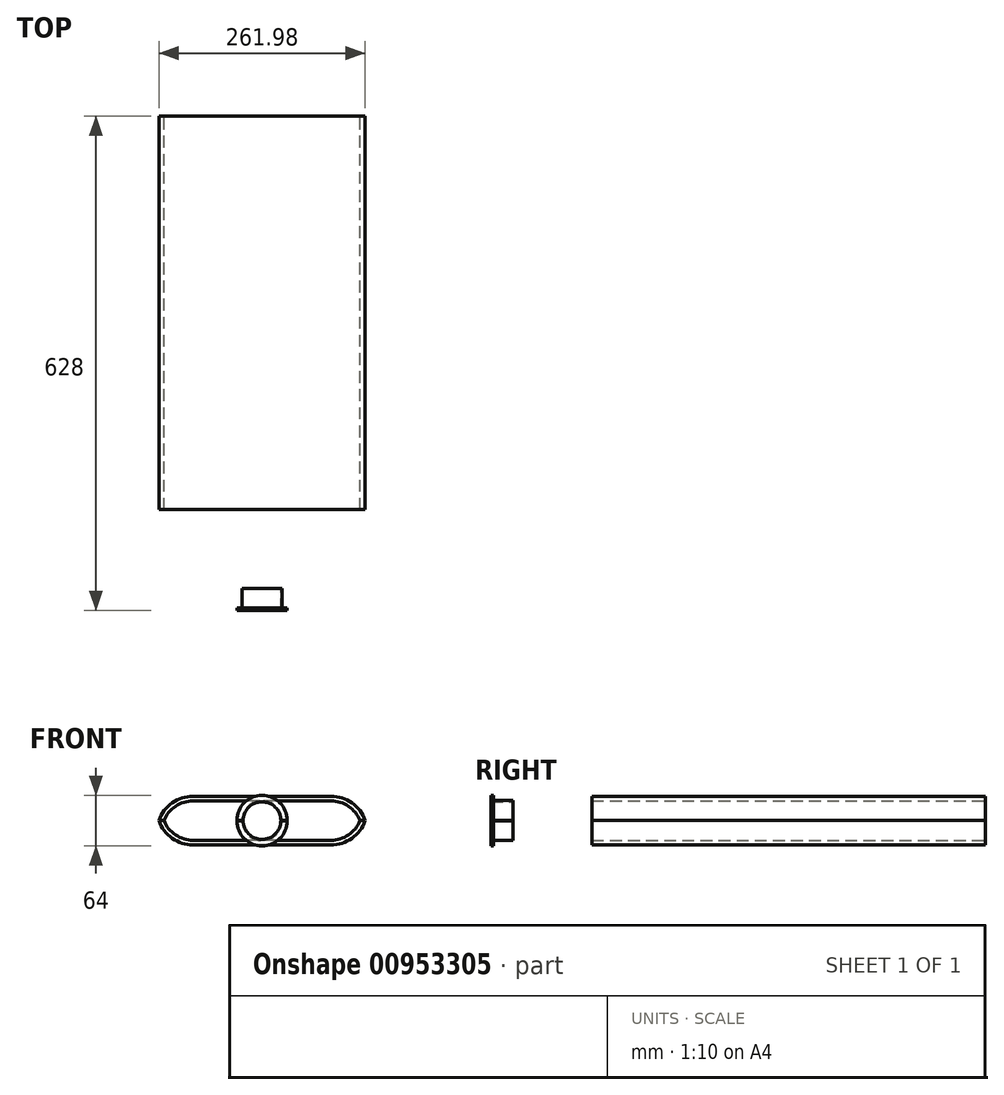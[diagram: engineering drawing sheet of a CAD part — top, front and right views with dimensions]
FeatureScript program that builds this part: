
annotation { "Feature Type Name" : "Feature", "Feature Type Description" : "" }
export const myFeature = defineFeature(function(context is Context, id is Id, definition is map)
    precondition{}
    {
        {
            var Q0;
            Q0=qCreatedBy(makeId("Front.planeOp"),FACE);
            var sketch = newSketch(context, id + "F0", { "sketchPlane" : qUnion([Q0])});
            skLineSegment(sketch, "E0", {"start": v(87.5, 25) * mm, "end": v(-87.5, 25) * mm});
            skLineSegment(sketch, "E1", {"start": v(0, 25) * mm, "end": v(0, 0) * mm, "construction": true});
            skArc(sketch, "E2", {"start": v(-87.5, 25) * mm, "mid": v(-109.86, 18.17) * mm, "end": v(-124.58, 0) * mm});
            skArc(sketch, "E3", {"start": v(124.58, 0) * mm, "mid": v(109.86, 18.17) * mm, "end": v(87.5, 25) * mm});
            skArc(sketch, "E4.0", {"start": v(-87.5, 31) * mm, "mid": v(-114.2, 22.46) * mm, "end": v(-130.99, 0) * mm});
            skLineSegment(sketch, "E4.1", {"start": v(87.5, 31) * mm, "end": v(-87.5, 31) * mm});
            skArc(sketch, "E4.2", {"start": v(130.99, 0) * mm, "mid": v(114.2, 22.46) * mm, "end": v(87.5, 31) * mm});
            skLineSegment(sketch, "E5", {"start": v(-124.58, 0) * mm, "end": v(-130.99, 0) * mm});
            skLineSegment(sketch, "E6", {"start": v(124.58, 0) * mm, "end": v(130.99, 0) * mm});
            skSolve(sketch);
        }
        {
            var Q0;
            Q0 = qSketchRegion(id + "F0", true);
            extrude(context, id + "F1", {"entities" : qUnion([Q0]), "endBound" : BoundingType.SYMMETRIC, "depth" : 500 * mm, "offsetDistance" : 25 * mm});
        }
        {
            var Q0;
            Q0=makeQuery(id+"F1.opExtrude","SWEPT_BODY",BODY,{"disambiguationData":[OSD([sQuery(id+"F0.wireOp",EDGE,"E0"),sQuery(id+"F0.wireOp",EDGE,"E2"),sQuery(id+"F0.wireOp",EDGE,"E3"),sQuery(id+"F0.wireOp",EDGE,"E4.0"),sQuery(id+"F0.wireOp",EDGE,"E4.1"),sQuery(id+"F0.wireOp",EDGE,"E4.2"),sQuery(id+"F0.wireOp",EDGE,"E5"),sQuery(id+"F0.wireOp",EDGE,"E6")])]});
            var Q1;
            Q1=makeQuery(id+"F1.opExtrude","SWEPT_FACE",FACE,{"disambiguationData":[OSD([sQuery(id+"F0.wireOp",EDGE,"E5")])]});
            mirror(context, id + "F2", {"entities" : qUnion([Q0]), "mirrorPlane" : qUnion([Q1])});
        }
        {
            var Q0;
            Q0=makeQuery(id+"F1.opExtrude","CAP_FACE",FACE,{"disambiguationData":[OSD([sQuery(id+"F0.wireOp",EDGE,"E0"),sQuery(id+"F0.wireOp",EDGE,"E2"),sQuery(id+"F0.wireOp",EDGE,"E3"),sQuery(id+"F0.wireOp",EDGE,"E4.0"),sQuery(id+"F0.wireOp",EDGE,"E4.1"),sQuery(id+"F0.wireOp",EDGE,"E4.2"),sQuery(id+"F0.wireOp",EDGE,"E5"),sQuery(id+"F0.wireOp",EDGE,"E6")])],"isStart":false});
            cPlane(context, id + "F3", {"entities" : qUnion([Q0]), "cplaneType" : CPlaneType.OFFSET, "offset" : 100 * mm, "width" : 150 * mm, "height" : 150 * mm});
        }
        {
            var Q0;
            Q0=qCreatedBy(id+"F3.planeOp",FACE);
            var sketch = newSketch(context, id + "F4", { "sketchPlane" : qUnion([Q0])});
            skCircle(sketch, "E7", {"center": v(0, 0) * mm, "radius": 25.4 * mm});
            skCircle(sketch, "E8", {"center": v(0, 0) * mm, "radius": 23.9 * mm});
            skSolve(sketch);
        }
        {
            var Q0;
            Q0 = qSketchRegion(id + "F4", true);
            extrude(context, id + "F5", {"entities" : qUnion([Q0]), "depth" : 25 * mm, "offsetDistance" : 25 * mm});
        }
        {
            var Q0;
            Q0=makeQuery(id+"F5.opExtrude","CAP_FACE",FACE,{"disambiguationData":[OSD([sQuery(id+"F4.wireOp",EDGE,"E7"),sQuery(id+"F4.wireOp",EDGE,"E8")])],"isStart":false});
            var sketch = newSketch(context, id + "F6", { "sketchPlane" : qUnion([Q0])});
            skCircle(sketch, "E9", {"center": v(0, 0) * mm, "radius": 32 * mm});
            skCircle(sketch, "E10", {"center": v(0, 0) * mm, "radius": 23.9 * mm});
            skSolve(sketch);
        }
        {
            var Q0;
            Q0 = qSketchRegion(id + "F6", true);
            extrude(context, id + "F7", {"entities" : qUnion([Q0]), "operationType" : NewBodyOperationType.ADD, "depth" : 3 * mm, "offsetDistance" : 25 * mm});
        }
        {
            var Q0;
            Q0=qCreatedBy(makeId("Right.planeOp"),FACE);
            var sketch = newSketch(context, id + "F8", { "sketchPlane" : qUnion([Q0])});
            skLineSegment(sketch, "E11", {"start": v(-250, 31) * mm, "end": v(-350, 25.4) * mm});
            skSolve(sketch);
        }
        {
            var Q0;
            Q0=qCreatedBy(makeId("Right.planeOp"),FACE);
            var sketch = newSketch(context, id + "F9", { "sketchPlane" : qUnion([Q0])});
            skLineSegment(sketch, "E12", {"start": v(-350, 0) * mm, "end": v(-378, 0) * mm});
            skLineSegment(sketch, "E13.0", {"start": v(-350, 0.1) * mm, "end": v(-378, 0.1) * mm});
            skLineSegment(sketch, "E14.0", {"start": v(-350, -0.1) * mm, "end": v(-378, -0.1) * mm});
            skLineSegment(sketch, "E15", {"start": v(-350, 0.1) * mm, "end": v(-350, -0.1) * mm});
            skLineSegment(sketch, "E16", {"start": v(-378, 0.1) * mm, "end": v(-378, -0.1) * mm});
            skSolve(sketch);
        }
        {
            var Q0;
            Q0 = qSketchRegion(id + "F9", true);
            extrude(context, id + "F10", {"entities" : qUnion([Q0]), "operationType" : NewBodyOperationType.REMOVE, "endBound" : BoundingType.THROUGH_ALL, "oppositeDirection" : true, "depth" : 25 * mm, "offsetDistance" : 25 * mm, "hasSecondDirection" : true, "secondDirectionBound" : SecondDirectionBoundingType.THROUGH_ALL, "secondDirectionOppositeDirection" : false, "secondDirectionDepth" : 25 * mm});
        }
    });
